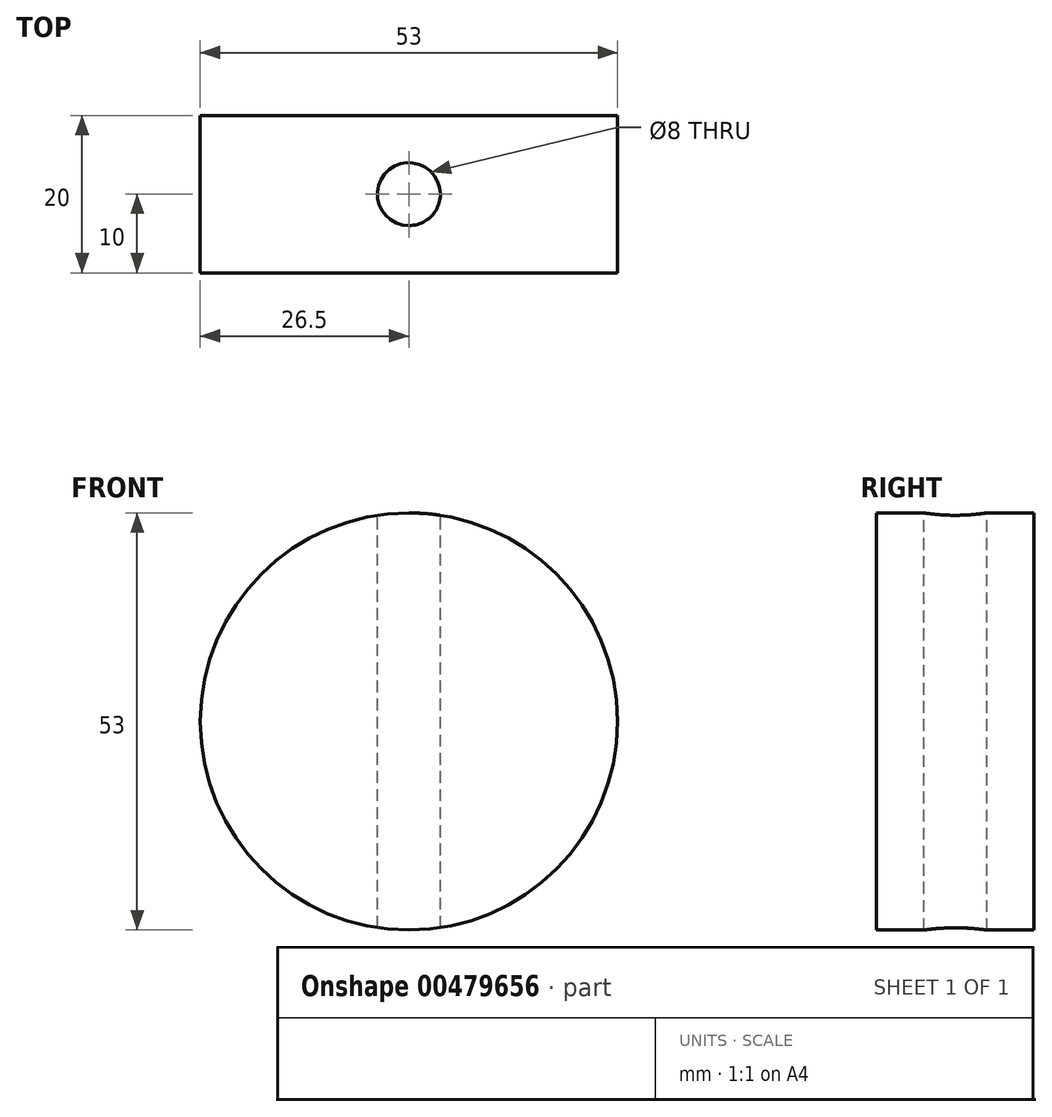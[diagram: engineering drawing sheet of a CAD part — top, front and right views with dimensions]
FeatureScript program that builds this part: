
annotation { "Feature Type Name" : "Feature", "Feature Type Description" : "" }
export const myFeature = defineFeature(function(context is Context, id is Id, definition is map)
    precondition{}
    {
        {
            var Q0;
            Q0=qCreatedBy(makeId("Front.planeOp"),FACE);
            var sketch = newSketch(context, id + "F0", { "sketchPlane" : qUnion([Q0])});
            skCircle(sketch, "E0", {"center": v(0, 0) * mm, "radius": 26.5 * mm});
            skPoint(sketch, "E1", {"position": v(-26.5, 0) * mm});
            skSolve(sketch);
        }
        {
            var Q0;
            Q0=makeQuery(id+"F0.imprint","IMPRINT",FACE,{"disambiguationData":[TD([[makeQuery(id+"F0.imprint","IMPRINT",EDGE,{"derivedFrom":sQuery(id+"F0.wireOp",EDGE,"E0")}),1.0]])]});
            extrude(context, id + "F1", {"entities" : qUnion([Q0]), "depth" : 20 * mm});
        }
        {
            var Q0;
            Q0=qCreatedBy(makeId("Top.planeOp"),FACE);
            var sketch = newSketch(context, id + "F2", { "sketchPlane" : qUnion([Q0])});
            skCircle(sketch, "E2", {"center": v(0, -10) * mm, "radius": 4 * mm});
            skSolve(sketch);
        }
        {
            var Q0;
            Q0 = qSketchRegion(id + "F2", true);
            extrude(context, id + "F3", {"entities" : qUnion([Q0]), "operationType" : NewBodyOperationType.REMOVE, "endBound" : BoundingType.THROUGH_ALL, "oppositeDirection" : true, "depth" : 50 * mm});
        }
        {
            var Q0;
            Q0 = qSketchRegion(id + "F2", true);
            extrude(context, id + "F4", {"entities" : qUnion([Q0]), "operationType" : NewBodyOperationType.REMOVE, "endBound" : BoundingType.THROUGH_ALL, "depth" : 25 * mm});
        }
    });
